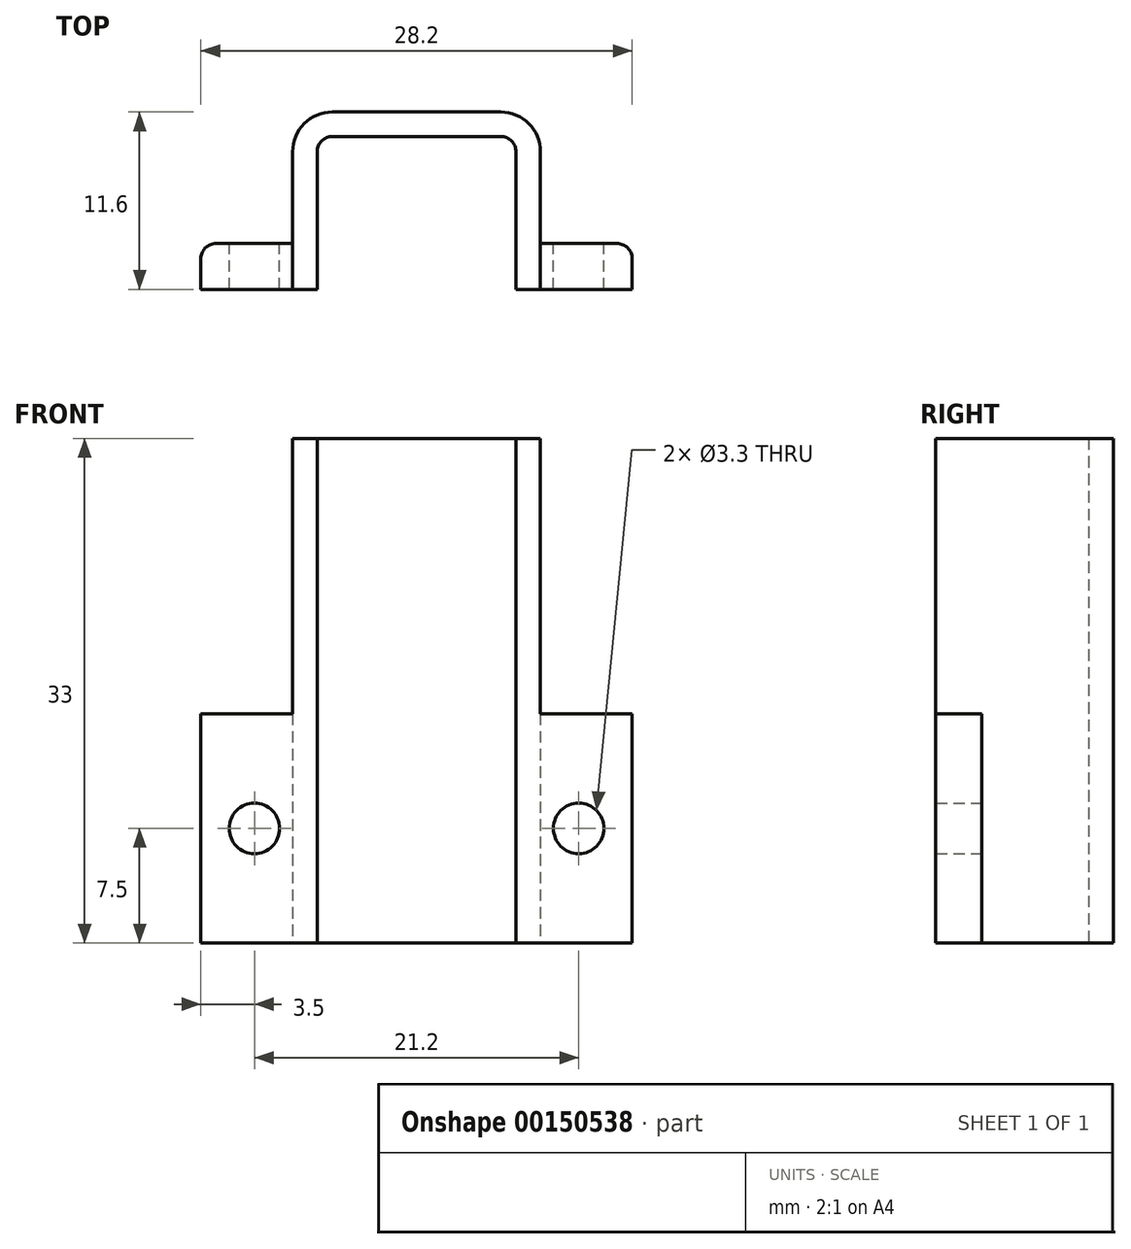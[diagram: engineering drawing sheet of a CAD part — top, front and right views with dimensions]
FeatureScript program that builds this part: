
annotation { "Feature Type Name" : "Feature", "Feature Type Description" : "" }
export const myFeature = defineFeature(function(context is Context, id is Id, definition is map)
    precondition{}
    {
        {
            assignVariable(context, id + "F0", {"name" : "thickness", "anyValue" : 1.6});
        }
        {
            var Q0;
            Q0=qCreatedBy(makeId("Top.planeOp"),FACE);
            var sketch = newSketch(context, id + "F1", { "sketchPlane" : qUnion([Q0])});
            skLineSegment(sketch, "E0", {"start": v(0, 0) * mm, "end": v(7.6, 0) * mm});
            skLineSegment(sketch, "E1", {"start": v(7.6, 0) * mm, "end": v(7.6, 10) * mm});
            skLineSegment(sketch, "E2", {"start": v(7.6, 10) * mm, "end": v(20.6, 10) * mm});
            skLineSegment(sketch, "E3", {"start": v(20.6, 10) * mm, "end": v(20.6, 0) * mm});
            skLineSegment(sketch, "E4", {"start": v(20.6, 0) * mm, "end": v(28.2, 0) * mm});
            skLineSegment(sketch, "E5", {"start": v(28.2, 0) * mm, "end": v(28.2, 3) * mm});
            skLineSegment(sketch, "E6", {"start": v(28.2, 3) * mm, "end": v(22.2, 3) * mm});
            skLineSegment(sketch, "E7", {"start": v(22.2, 3) * mm, "end": v(22.2, 11.6) * mm});
            skLineSegment(sketch, "E8", {"start": v(22.2, 11.6) * mm, "end": v(6, 11.6) * mm});
            skLineSegment(sketch, "E9", {"start": v(6, 11.6) * mm, "end": v(6, 3) * mm});
            skLineSegment(sketch, "E10", {"start": v(6, 3) * mm, "end": v(0, 3) * mm});
            skLineSegment(sketch, "E11", {"start": v(0, 3) * mm, "end": v(0, 0) * mm});
            skSolve(sketch);
        }
        {
            var Q0;
            Q0=makeQuery(id+"F1.imprint","IMPRINT",FACE,{"disambiguationData":[TD([[makeQuery(id+"F1.imprint","IMPRINT",EDGE,{"derivedFrom":sQuery(id+"F1.wireOp",EDGE,"E0")}),1.0]])]});
            extrude(context, id + "F2", {"entities" : qUnion([Q0]), "depth" : 15 * mm});
        }
        {
            var Q0;
            Q0=makeQuery(id+"F2.opExtrude","CAP_FACE",FACE,{"disambiguationData":[OSD([sQuery(id+"F1.wireOp",EDGE,"E0"),sQuery(id+"F1.wireOp",EDGE,"E1"),sQuery(id+"F1.wireOp",EDGE,"E2"),sQuery(id+"F1.wireOp",EDGE,"E3"),sQuery(id+"F1.wireOp",EDGE,"E4"),sQuery(id+"F1.wireOp",EDGE,"E5"),sQuery(id+"F1.wireOp",EDGE,"E6"),sQuery(id+"F1.wireOp",EDGE,"E7"),sQuery(id+"F1.wireOp",EDGE,"E8"),sQuery(id+"F1.wireOp",EDGE,"E9"),sQuery(id+"F1.wireOp",EDGE,"E10"),sQuery(id+"F1.wireOp",EDGE,"E11")])],"isStart":false});
            var sketch = newSketch(context, id + "F3", { "sketchPlane" : qUnion([Q0])});
            skLineSegment(sketch, "E12", {"start": v(7.6, 0) * mm, "end": v(7.6, 10) * mm});
            skLineSegment(sketch, "E13", {"start": v(7.6, 10) * mm, "end": v(20.6, 10) * mm});
            skLineSegment(sketch, "E14", {"start": v(20.6, 10) * mm, "end": v(20.6, 0) * mm});
            skLineSegment(sketch, "E15", {"start": v(20.6, 0) * mm, "end": v(22.2, 0) * mm});
            skLineSegment(sketch, "E16", {"start": v(22.2, 0) * mm, "end": v(22.2, 11.6) * mm});
            skLineSegment(sketch, "E17", {"start": v(22.2, 11.6) * mm, "end": v(6, 11.6) * mm});
            skLineSegment(sketch, "E18", {"start": v(6, 11.6) * mm, "end": v(6, 0) * mm});
            skLineSegment(sketch, "E19", {"start": v(6, 0) * mm, "end": v(7.6, 0) * mm});
            skSolve(sketch);
        }
        {
            var Q0;
            Q0=makeQuery(id+"F3.imprint","IMPRINT",FACE,{"disambiguationData":[TD([[makeQuery(id+"F3.imprint","IMPRINT",EDGE,{"derivedFrom":sQuery(id+"F3.wireOp",EDGE,"E12")}),1.0]])]});
            extrude(context, id + "F4", {"entities" : qUnion([Q0]), "operationType" : NewBodyOperationType.ADD, "depth" : 18 * mm});
        }
        {
            var Q0;
            Q0=makeQuery(id+"F2.opExtrude","SWEPT_FACE",FACE,{"disambiguationData":[OSD([sQuery(id+"F1.wireOp",EDGE,"E10")])]});
            var sketch = newSketch(context, id + "F5", { "sketchPlane" : qUnion([Q0])});
            skCircle(sketch, "E20", {"center": v(-3.5, 7.5) * mm, "radius": 1.42 * mm});
            skSolve(sketch);
        }
        {
            var Q0;
            Q0=sQuery(id+"F5.wireOp",VERTEX,"E20.center");
            var Q1;
            Q1=makeQuery(id+"F2.opExtrude","SWEPT_BODY",BODY,{"disambiguationData":[OSD([sQuery(id+"F1.wireOp",EDGE,"E0"),sQuery(id+"F1.wireOp",EDGE,"E1"),sQuery(id+"F1.wireOp",EDGE,"E2"),sQuery(id+"F1.wireOp",EDGE,"E3"),sQuery(id+"F1.wireOp",EDGE,"E4"),sQuery(id+"F1.wireOp",EDGE,"E5"),sQuery(id+"F1.wireOp",EDGE,"E6"),sQuery(id+"F1.wireOp",EDGE,"E7"),sQuery(id+"F1.wireOp",EDGE,"E8"),sQuery(id+"F1.wireOp",EDGE,"E9"),sQuery(id+"F1.wireOp",EDGE,"E10"),sQuery(id+"F1.wireOp",EDGE,"E11")])]});
            hole(context, id + "F6", {"style" : HoleStyle.SIMPLE, "endStyle" : HoleEndStyle.THROUGH, "standardTappedOrClearance" : lookupTablePath({ "standard" : "ISO", "fit" : "Normal", "size" : "M3", "type" : "Clearance" }), "standardBlindInLast" : lookupTablePath({ "fit" : "Standard", "standard" : "ISO", "size" : "M3", "type" : "Clearance" }), "holeDiameter" : 3.3 * mm, "locations" : qUnion([Q0]), "scope" : qUnion([Q1]), "isTappedThrough" : true});
        }
        {
            var Q0;
            Q0=makeQuery(id+"F2.opExtrude","SWEPT_FACE",FACE,{"disambiguationData":[OSD([sQuery(id+"F1.wireOp",EDGE,"E6")])]});
            var sketch = newSketch(context, id + "F7", { "sketchPlane" : qUnion([Q0])});
            skCircle(sketch, "E21", {"center": v(-24.7, 7.5) * mm, "radius": 1.33 * mm});
            skSolve(sketch);
        }
        {
            var Q0;
            Q0=sQuery(id+"F7.wireOp",VERTEX,"E21.center");
            var Q1;
            Q1=makeQuery(id+"F2.opExtrude","SWEPT_BODY",BODY,{"disambiguationData":[OSD([sQuery(id+"F1.wireOp",EDGE,"E0"),sQuery(id+"F1.wireOp",EDGE,"E1"),sQuery(id+"F1.wireOp",EDGE,"E2"),sQuery(id+"F1.wireOp",EDGE,"E3"),sQuery(id+"F1.wireOp",EDGE,"E4"),sQuery(id+"F1.wireOp",EDGE,"E5"),sQuery(id+"F1.wireOp",EDGE,"E6"),sQuery(id+"F1.wireOp",EDGE,"E7"),sQuery(id+"F1.wireOp",EDGE,"E8"),sQuery(id+"F1.wireOp",EDGE,"E9"),sQuery(id+"F1.wireOp",EDGE,"E10"),sQuery(id+"F1.wireOp",EDGE,"E11")])]});
            hole(context, id + "F8", {"style" : HoleStyle.SIMPLE, "endStyle" : HoleEndStyle.THROUGH, "standardTappedOrClearance" : lookupTablePath({ "standard" : "ISO", "fit" : "Normal", "size" : "M3", "type" : "Clearance" }), "standardBlindInLast" : lookupTablePath({ "fit" : "Standard", "standard" : "ISO", "size" : "M3", "type" : "Clearance" }), "holeDiameter" : 3.3 * mm, "locations" : qUnion([Q0]), "scope" : qUnion([Q1]), "isTappedThrough" : true});
        }
        {
            var Q0;
            Q0=makeQuery(id+"F4.boolean.opBoolean","MERGE",EDGE,{"derivedFrom":[makeQuery(id+"F2.opExtrude","SWEPT_EDGE",EDGE,{"disambiguationData":[OSD([sQuery(id+"F1.wireOp",EDGE,"E2"),sQuery(id+"F1.wireOp",EDGE,"E3")])]}),makeQuery(id+"F4.opExtrude","SWEPT_EDGE",EDGE,{"disambiguationData":[OSD([sQuery(id+"F3.wireOp",EDGE,"E13"),sQuery(id+"F3.wireOp",EDGE,"E14")])]})]});
            var Q1;
            Q1=makeQuery(id+"F4.boolean.opBoolean","MERGE",EDGE,{"derivedFrom":[makeQuery(id+"F2.opExtrude","SWEPT_EDGE",EDGE,{"disambiguationData":[OSD([sQuery(id+"F1.wireOp",EDGE,"E1"),sQuery(id+"F1.wireOp",EDGE,"E2")])]}),makeQuery(id+"F4.opExtrude","SWEPT_EDGE",EDGE,{"disambiguationData":[OSD([sQuery(id+"F3.wireOp",EDGE,"E12"),sQuery(id+"F3.wireOp",EDGE,"E13")])]})]});
            var Q2;
            Q2=makeQuery(id+"F2.opExtrude","SWEPT_EDGE",EDGE,{"disambiguationData":[OSD([sQuery(id+"F1.wireOp",EDGE,"E5"),sQuery(id+"F1.wireOp",EDGE,"E6")])]});
            var Q3;
            Q3=makeQuery(id+"F2.opExtrude","SWEPT_EDGE",EDGE,{"disambiguationData":[OSD([sQuery(id+"F1.wireOp",EDGE,"E10"),sQuery(id+"F1.wireOp",EDGE,"E11")])]});
            fillet(context, id + "F9", {"entities" : qUnion([Q0, Q1, Q2, Q3]), "radius" : 1 * mm, "tangentPropagation" : true, "allowEdgeOverflow" : false});
        }
        {
            var Q0;
            Q0=makeQuery(id+"F4.boolean.opBoolean","MERGE",EDGE,{"derivedFrom":[makeQuery(id+"F2.opExtrude","SWEPT_EDGE",EDGE,{"disambiguationData":[OSD([sQuery(id+"F1.wireOp",EDGE,"E8"),sQuery(id+"F1.wireOp",EDGE,"E9")])]}),makeQuery(id+"F4.opExtrude","SWEPT_EDGE",EDGE,{"disambiguationData":[OSD([sQuery(id+"F3.wireOp",EDGE,"E17"),sQuery(id+"F3.wireOp",EDGE,"E18")])]})]});
            var Q1;
            Q1=makeQuery(id+"F4.boolean.opBoolean","MERGE",EDGE,{"derivedFrom":[makeQuery(id+"F2.opExtrude","SWEPT_EDGE",EDGE,{"disambiguationData":[OSD([sQuery(id+"F1.wireOp",EDGE,"E7"),sQuery(id+"F1.wireOp",EDGE,"E8")])]}),makeQuery(id+"F4.opExtrude","SWEPT_EDGE",EDGE,{"disambiguationData":[OSD([sQuery(id+"F3.wireOp",EDGE,"E16"),sQuery(id+"F3.wireOp",EDGE,"E17")])]})]});
            fillet(context, id + "F10", {"entities" : qUnion([Q0, Q1]), "radius" : (getVariable(context, 'thickness') + 1) * mm, "tangentPropagation" : true, "allowEdgeOverflow" : false});
        }
    });
